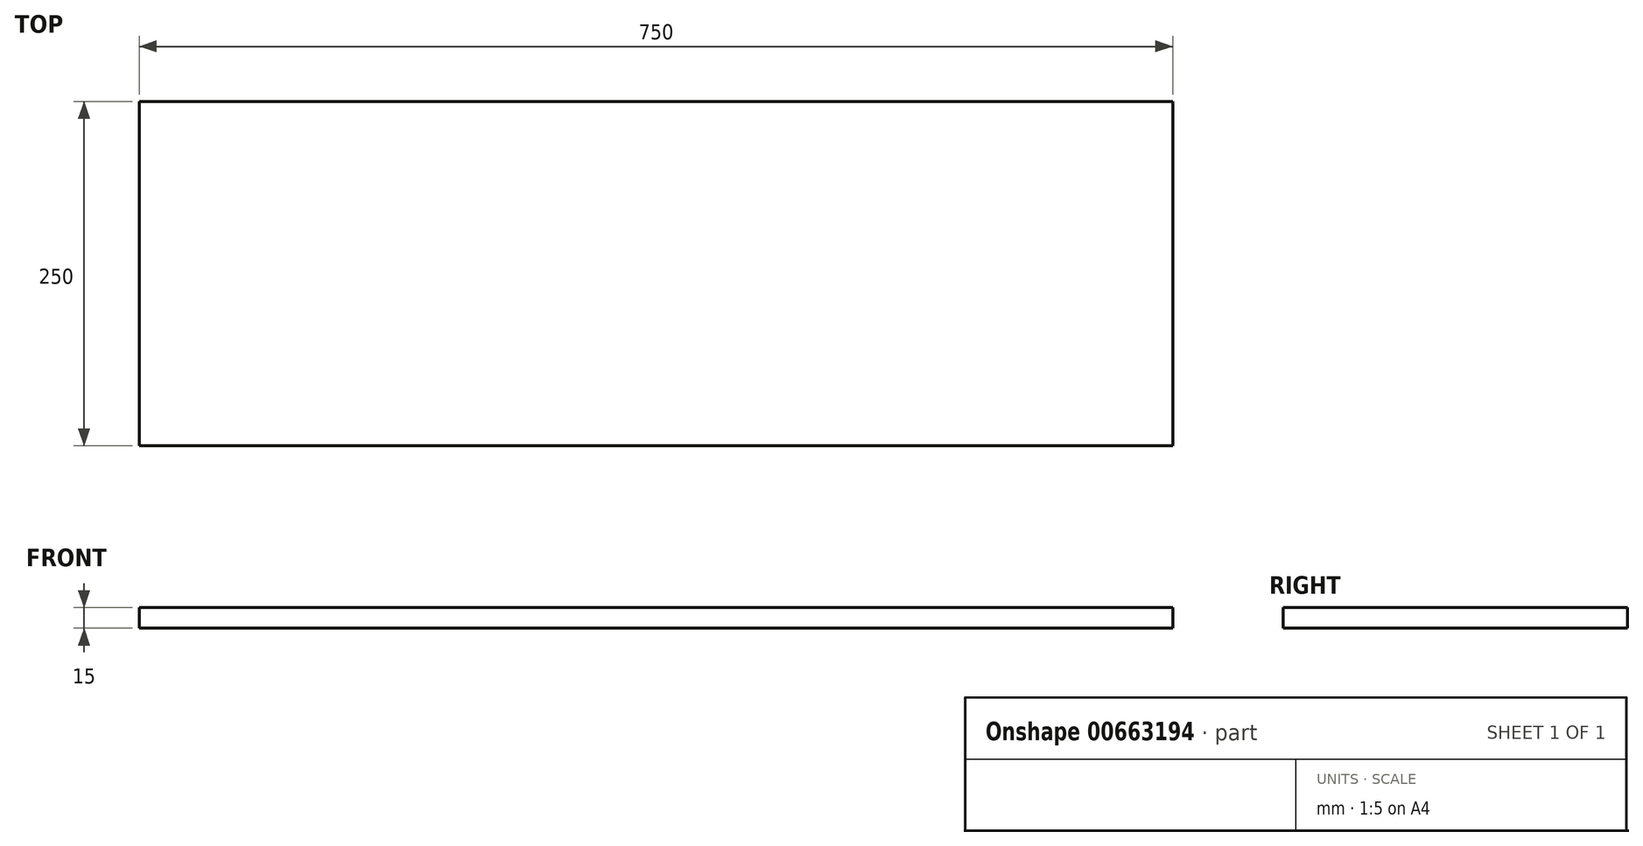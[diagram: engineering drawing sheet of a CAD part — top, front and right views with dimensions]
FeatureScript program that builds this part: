
annotation { "Feature Type Name" : "Feature", "Feature Type Description" : "" }
export const myFeature = defineFeature(function(context is Context, id is Id, definition is map)
    precondition{}
    {
        {
            var Q0;
            Q0=qCreatedBy(makeId("Top.planeOp"),FACE);
            var sketch = newSketch(context, id + "F0", { "sketchPlane" : qUnion([Q0])});
            skLineSegment(sketch, "E0.bottom", {"start": v(375, 125) * mm, "end": v(-375, 125) * mm});
            skLineSegment(sketch, "E0.top", {"start": v(375, -125) * mm, "end": v(-375, -125) * mm});
            skLineSegment(sketch, "E0.left", {"start": v(375, 125) * mm, "end": v(375, -125) * mm});
            skLineSegment(sketch, "E0.right", {"start": v(-375, 125) * mm, "end": v(-375, -125) * mm});
            skPoint(sketch, "E0.middle", {"position": v(0, 0) * mm});
            skSolve(sketch);
        }
        {
            var Q0;
            Q0 = qSketchRegion(id + "F0", true);
            extrude(context, id + "F1", {"entities" : qUnion([Q0]), "endBound" : BoundingType.SYMMETRIC, "depth" : 15 * mm, "offsetDistance" : 25 * mm});
        }
    });
